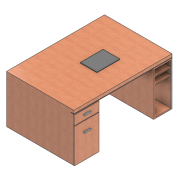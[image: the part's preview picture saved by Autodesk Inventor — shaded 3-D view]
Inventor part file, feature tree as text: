
AUTODESK INVENTOR PART (.ipt)
format: ipt  version: 2020.2 (Build 242310000, 310)  size: 341,504 bytes
history: native  units: mm
features: sketch x13, plane x12, extrude x10, shell x1, loft x1
ambient origin geometry x8: Origin, YZ Plane, XZ Plane, XY Plane, X Axis, Y Axis, Z Axis, Center Point
bodies: Solid1 (feature_tree), Solid2 (feature_tree), Solid3 (feature_tree), Solid4 (feature_tree), Solid5 (feature_tree)
feature tree (37):
  extrude  "Extrusion1"  Depth=1600.0mm
  plane  "Work Plane1"
  extrude  "Extrusion2"  Depth=400.0mm
  plane  "Work Plane2"
  extrude  "Extrusion3"  Depth=720.0mm TaperAngle=0.0deg
  plane  "Work Plane3"
  extrude  "Extrusion4"  Depth=1050.0mm
  plane  "Work Plane4"
  plane  "Work Plane5"
  sketch  "Sketch6"  dims[d9=60.0mm d10=0.0mm d11=10.0mm]
  extrude  "Extrusion5"  Depth=10.0mm
  extrude  "Extrusion6"  TaperAngle=0.0deg  [1 undecoded]
  plane  "Work Plane6"
  sketch  "Sketch9"  dims[d16=5.0mm d17=10.0mm d18=0.0mm]
  shell  "Shell1"  Thickness=155.0mm
  extrude  "Extrusion7"  Depth=10.0mm TaperAngle=0.0deg
  plane  "Work Plane7"
  extrude  "Extrusion8"  TaperAngle=0.0deg  [1 undecoded]
  plane  "Work Plane8"
  sketch  "Sketch11"  dims[d30=20.0mm d33=20.0mm]
  plane  "Work Plane9"
  sketch  "Sketch12"  dims[d34=15.0mm d35=0.0mm d36=15.0mm d37=0.0mm]
  plane  "Work Plane10"
  loft  "Loft1"
  plane  "Work Plane11"
  extrude  "Extrusion9"  Depth=15.0mm TaperAngle=0.0deg
  plane  "Work Plane12"
  extrude  "Extrusion10"  Depth=20.0mm
  sketch  "Sketch1"  dims[d0=1100.0mm d1=1600.0mm]
  sketch  "Sketch2"  dims[d2=85.0mm d3=400.0mm]
  sketch  "Sketch3"  dims[d4=300.0mm d5=720.0mm d6=0.0mm]
  sketch  "Sketch4"  dims[d7=0.0mm d8=1050.0mm]
  sketch  "Sketch7"  dims[d12=50.0mm d13=0.0mm d14=0.0mm d15=155.0mm]
  sketch  "Sketch10"  dims[d19=0.0mm d20=0.0mm]
  sketch  "Sketch13"  dims[d38=0.0mm d40=20.0mm]
  sketch  "Sketch14"  dims[d42=15.0mm]
  sketch  "Sketch15"  dims[d44=15.0mm d45=1100.0mm d46=0.0mm d47=0.0mm d48=9.0mm d49=0.0mm d50=0.0mm d51=255.0mm d52=358.5mm d53=9.0mm d61=3.5mm d62=10.0mm d63=90.0deg d64=0.0mm d65=90.0deg d66=10.0mm d67=90.0deg d68=0.1mm d69=3.0mm d70=4.0mm d71=0.0mm d72=0.0mm d73=4.0mm d74=0.0mm]
note: 2 required parameter values undecoded (feature->parameter linkage not recoverable at this tier; creation-order binding heuristic only, values carry confidence <= 0.55)
